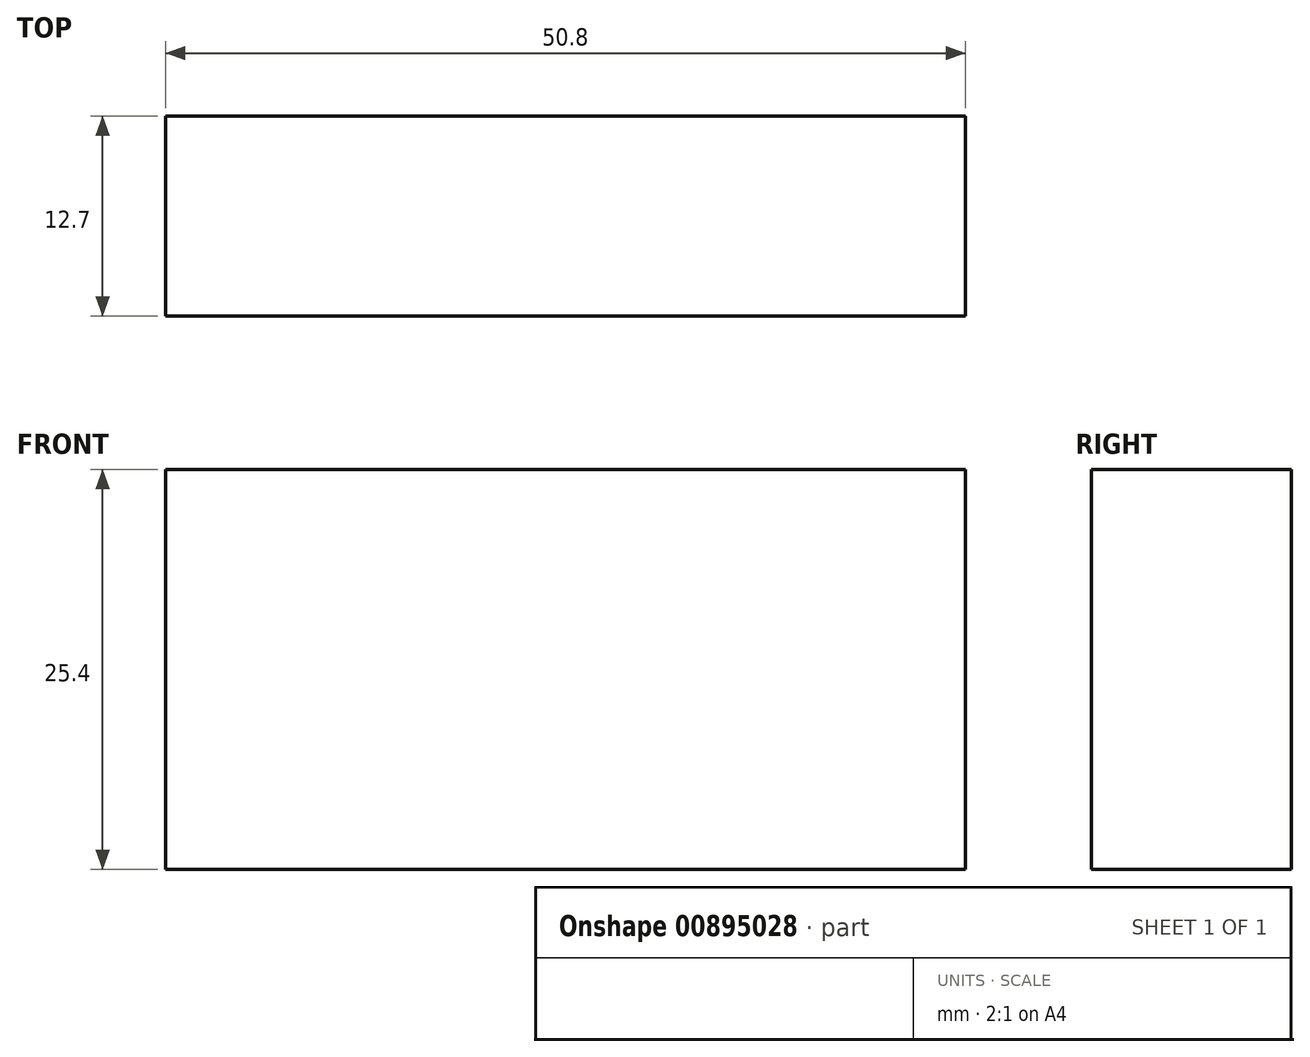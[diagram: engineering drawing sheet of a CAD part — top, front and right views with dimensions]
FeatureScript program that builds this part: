
annotation { "Feature Type Name" : "Feature", "Feature Type Description" : "" }
export const myFeature = defineFeature(function(context is Context, id is Id, definition is map)
    precondition{}
    {
        {
            var Q0;
            Q0=qCreatedBy(makeId("Top.planeOp"),FACE);
            var sketch = newSketch(context, id + "F0", { "sketchPlane" : qUnion([Q0])});
            skLineSegment(sketch, "E0.bottom", {"start": v(-101.2, -13.72) * mm, "end": v(-152, -13.72) * mm});
            skLineSegment(sketch, "E0.top", {"start": v(-101.2, -1.02) * mm, "end": v(-152, -1.02) * mm});
            skLineSegment(sketch, "E0.left", {"start": v(-101.2, -13.72) * mm, "end": v(-101.2, -1.02) * mm});
            skLineSegment(sketch, "E0.right", {"start": v(-152, -13.72) * mm, "end": v(-152, -1.02) * mm});
            skPoint(sketch, "E0.middle", {"position": v(-126.6, -7.37) * mm});
            skSolve(sketch);
        }
        {
            var Q0;
            Q0=qSketchRegion(id+"F0",true);
            extrude(context, id + "F1", {"entities" : qUnion([Q0]), "depth" : 25.4 * mm, "offsetDistance" : 25.4 * mm});
        }
    });
